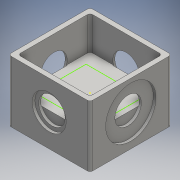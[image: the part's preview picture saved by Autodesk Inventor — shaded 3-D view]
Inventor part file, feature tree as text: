
AUTODESK INVENTOR PART (.ipt)
format: ipt  version: 2016 (Build 200138000, 138)  size: 180,224 bytes
history: native  units: mm
features: sketch x6, extrude x5, mirror x2, pattern_circular x1
ambient origin geometry x8: Origin, YZ Plane, XZ Plane, XY Plane, X Axis, Y Axis, Z Axis, Center Point
bodies: Solid1 (feature_tree)
feature tree (14):
  extrude  "Extrusion1"  Depth=60.0mm
  extrude  "Extrusion2"  Depth=30.0mm
  extrude  "Extrusion3"  Depth=45.0mm TaperAngle=0.0deg
  mirror  "Mirror1"
  extrude  "Extrusion4"  Depth=53.0mm
  mirror  "Mirror2"
  extrude  "Extrusion5"  Depth=26.5mm
  pattern_circular  "Circular Pattern1"  [2 undecoded]
  sketch  "Sketch6"  dims[d11=2.0mm d12=24.5mm d13=0.0mm d14=37.0mm d15=23.5mm d16=2.0mm d17=0.0mm d18=25.0mm d19=23.5mm d20=2.0mm d21=0.0mm d22=19.5mm d23=2.0mm d24=0.0mm d25=40.0mm d26=360.0deg]
  sketch  "Sketch1"  dims[d0=60.0mm d1=60.0mm]
  sketch  "Sketch2"  dims[d2=30.0mm d3=30.0mm]
  sketch  "Sketch3"  dims[d4=2.0mm d5=45.0mm d6=0.0mm]
  sketch  "Sketch4"  dims[d7=53.0mm d8=53.0mm]
  sketch  "Sketch5"  dims[d9=26.5mm d10=26.5mm]
note: 2 required parameter values undecoded (feature->parameter linkage not recoverable at this tier; creation-order binding heuristic only, values carry confidence <= 0.55)
